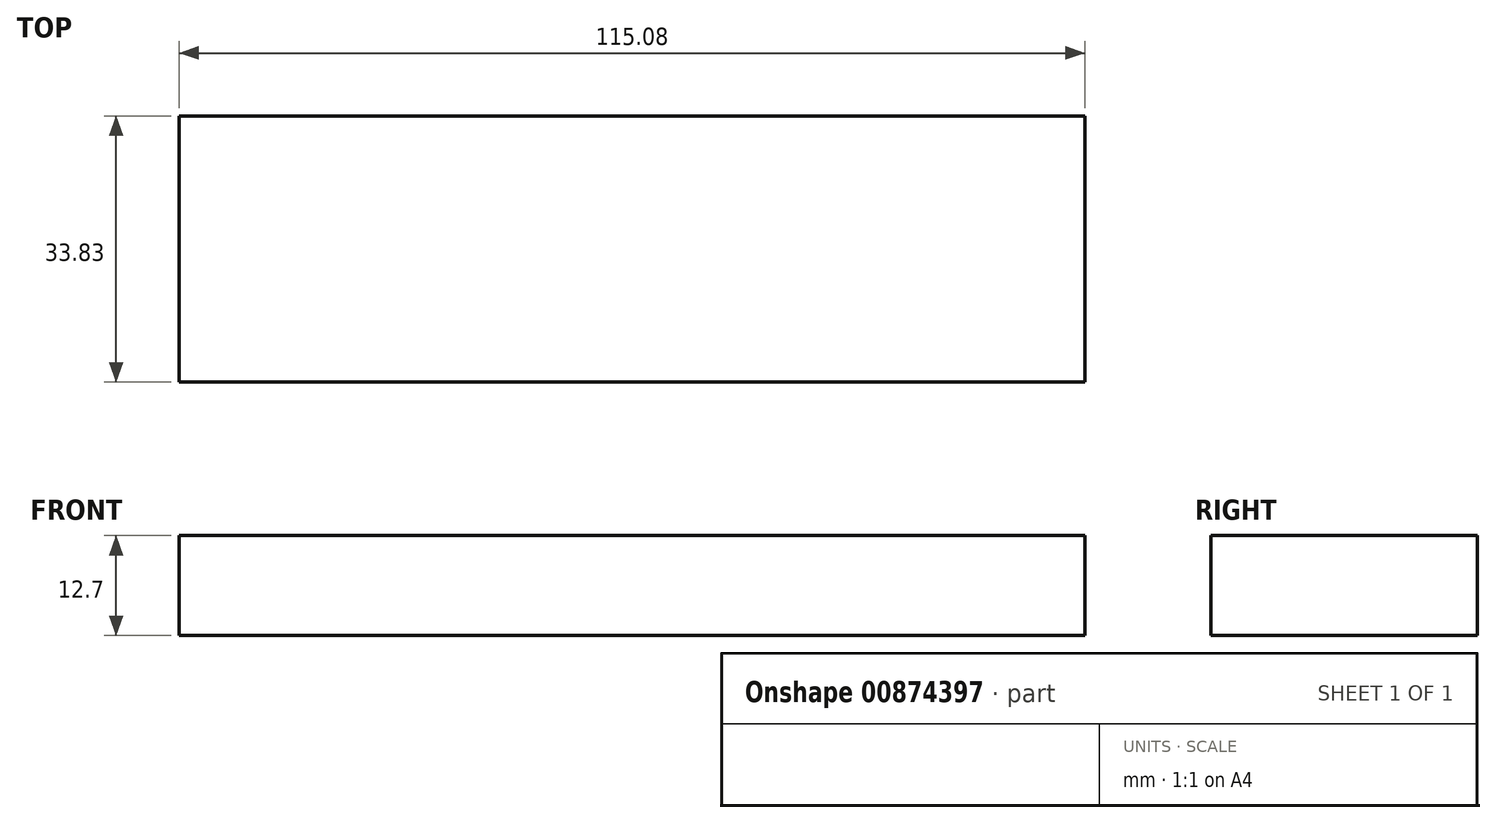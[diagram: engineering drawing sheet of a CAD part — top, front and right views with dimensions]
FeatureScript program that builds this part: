
annotation { "Feature Type Name" : "Feature", "Feature Type Description" : "" }
export const myFeature = defineFeature(function(context is Context, id is Id, definition is map)
    precondition{}
    {
        {
            var Q0;
            Q0=qCreatedBy(makeId("Top.planeOp"),FACE);
            var sketch = newSketch(context, id + "F0", { "sketchPlane" : qUnion([Q0])});
            skLineSegment(sketch, "E0.bottom", {"start": v(-64.25, 33.83) * mm, "end": v(50.83, 33.83) * mm});
            skLineSegment(sketch, "E0.top", {"start": v(-64.25, 0) * mm, "end": v(50.83, 0) * mm});
            skLineSegment(sketch, "E0.left", {"start": v(-64.25, 33.83) * mm, "end": v(-64.25, 0) * mm});
            skLineSegment(sketch, "E0.right", {"start": v(50.83, 33.83) * mm, "end": v(50.83, 0) * mm});
            skSolve(sketch);
        }
        {
            var Q0;
            Q0=makeQuery(id+"F0.imprint","IMPRINT",FACE,{"disambiguationData":[TD([[makeQuery(id+"F0.imprint","IMPRINT",EDGE,{"derivedFrom":sQuery(id+"F0.wireOp",EDGE,"E0.bottom")}),-1.0]])]});
            extrude(context, id + "F1", {"entities" : qUnion([Q0]), "depth" : 12.7 * mm, "offsetDistance" : 25.4 * mm});
        }
    });
